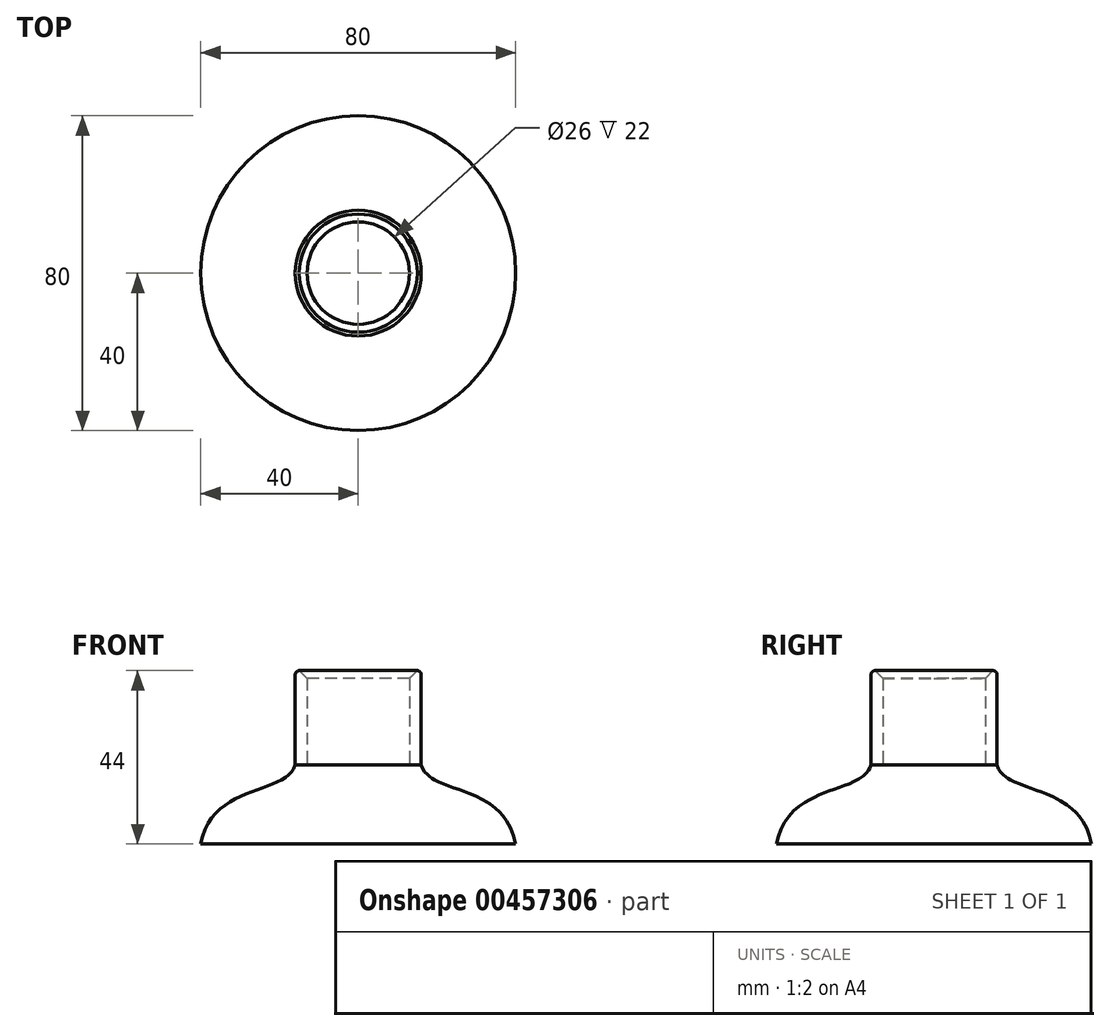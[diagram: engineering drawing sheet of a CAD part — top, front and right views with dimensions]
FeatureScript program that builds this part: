
annotation { "Feature Type Name" : "Feature", "Feature Type Description" : "" }
export const myFeature = defineFeature(function(context is Context, id is Id, definition is map)
    precondition{}
    {
        {
            var Q0;
            Q0=qCreatedBy(makeId("Top.planeOp"),FACE);
            var sketch = newSketch(context, id + "F0", { "sketchPlane" : qUnion([Q0])});
            skCircle(sketch, "E0", {"center": v(0, 0) * mm, "radius": 13 * mm});
            skCircle(sketch, "E1", {"center": v(0, 0) * mm, "radius": 16 * mm});
            skSolve(sketch);
        }
        {
            var Q0;
            Q0 = qSketchRegion(id + "F0", true);
            extrude(context, id + "F1", {"entities" : qUnion([Q0]), "depth" : 24 * mm});
        }
        {
            var Q0;
            Q0=makeQuery(id+"F1.opExtrude","SWEPT_BODY",BODY,{"disambiguationData":[OSD([sQuery(id+"F0.wireOp",EDGE,"E0"),sQuery(id+"F0.wireOp",EDGE,"E1")])]});
            transform(context, id + "F2", {"entities" : qUnion([Q0]), "transformType" : TransformType.TRANSLATION_3D, "dx" : 0 * mm, "dy" : 0 * mm, "dz" : 20 * mm, "makeCopy" : false});
        }
        {
            var Q0;
            Q0=qCreatedBy(makeId("Front.planeOp"),FACE);
            var sketch = newSketch(context, id + "F3", { "sketchPlane" : qUnion([Q0])});
            skLineSegment(sketch, "E2", {"start": v(0, 0) * mm, "end": v(0, 20) * mm});
            skLineSegment(sketch, "E3", {"start": v(0, 20) * mm, "end": v(16, 20) * mm});
            skLineSegment(sketch, "E4", {"start": v(0, 0) * mm, "end": v(40, 0) * mm});
            skFitSpline(sketch, "E5", {"points": [v(16, 20) * mm, v(40, 0) * mm], "startDerivative": vector(6.9, -23.05) * mm, "endDerivative": vector(8.63, -46.7) * mm});
            skSolve(sketch);
        }
        {
            var Q0;
            Q0=makeQuery(id+"F3.imprint","IMPRINT",FACE,{"disambiguationData":[TD([[makeQuery(id+"F3.imprint","IMPRINT",EDGE,{"derivedFrom":sQuery(id+"F3.wireOp",EDGE,"E2")}),-1.0]])]});
            var Q1;
            Q1=sQuery(id+"F3.wireOp",EDGE,"E2");
            revolve(context, id + "F4", {"operationType" : NewBodyOperationType.ADD, "entities" : qUnion([Q0]), "axis" : qUnion([Q1]), "revolveType" : RevolveType.FULL});
        }
        {
            var Q0;
            Q0=makeQuery(id+"F1.opExtrude","CAP_EDGE",EDGE,{"disambiguationData":[OSD([sQuery(id+"F0.wireOp",EDGE,"E1")])],"isStart":false});
            fillet(context, id + "F5", {"entities" : qUnion([Q0]), "radius" : 1 * mm, "tangentPropagation" : true, "allowEdgeOverflow" : false});
        }
        {
            var Q0;
            Q0=makeQuery(id+"F1.opExtrude","CAP_EDGE",EDGE,{"disambiguationData":[OSD([sQuery(id+"F0.wireOp",EDGE,"E0")])],"isStart":false});
            chamfer(context, id + "F6", {"entities" : qUnion([Q0]), "width" : 2 * mm, "tangentPropagation" : true});
        }
    });
